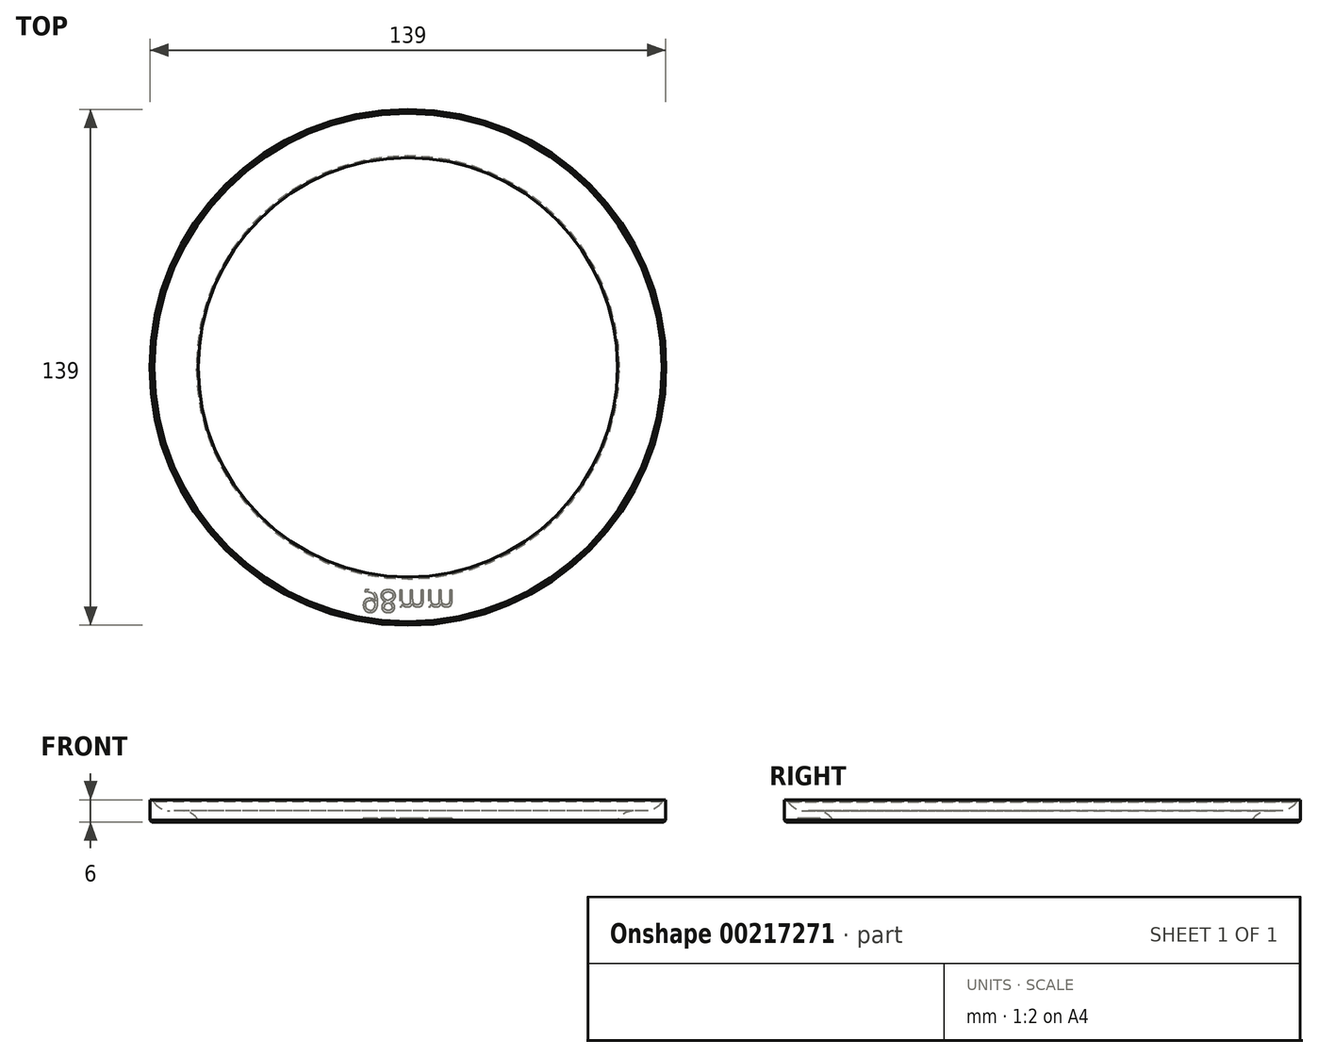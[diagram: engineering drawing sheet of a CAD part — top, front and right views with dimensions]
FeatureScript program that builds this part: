
annotation { "Feature Type Name" : "Feature", "Feature Type Description" : "" }
export const myFeature = defineFeature(function(context is Context, id is Id, definition is map)
    precondition{}
    {
        {
            var Q0;
            Q0=qCreatedBy(makeId("Front.planeOp"),FACE);
            var sketch = newSketch(context, id + "F0", { "sketchPlane" : qUnion([Q0])});
            skLineSegment(sketch, "E0", {"start": v(-69.5, 6) * mm, "end": v(-69.5, 0) * mm});
            skLineSegment(sketch, "E1", {"start": v(-69.5, 0) * mm, "end": v(-56.5, 0) * mm});
            skLineSegment(sketch, "E2", {"start": v(-56.5, 0) * mm, "end": v(-56.5, 3) * mm});
            skLineSegment(sketch, "E3", {"start": v(-56.5, 3) * mm, "end": v(-68.5, 3) * mm});
            skLineSegment(sketch, "E4", {"start": v(-68.5, 3) * mm, "end": v(-68.5, 6) * mm});
            skLineSegment(sketch, "E5", {"start": v(-68.5, 6) * mm, "end": v(-69.5, 6) * mm});
            skLineSegment(sketch, "E6", {"start": v(0, 62.77) * mm, "end": v(0, -27.64) * mm, "construction": true});
            skSolve(sketch);
        }
        {
            var Q0;
            Q0=qSketchRegion(id+"F0",true);
            var Q1;
            Q1=qSketchRegion(id+"F3",true);
            var Q2;
            Q2=sQuery(id+"F0.wireOp",EDGE,"E6");
            revolve(context, id + "F1", {"surfaceOperationType" : NewSurfaceOperationType.NEW, "entities" : qUnion([Q0, Q1]), "axis" : qUnion([Q2]), "revolveType" : RevolveType.FULL});
        }
        {
            var Q0;
            Q0=makeQuery(id+"F1.opRevolve","SWEPT_FACE",FACE,{"disambiguationData":[OSD([sQuery(id+"F0.wireOp",EDGE,"E1")])]});
            var Q1;
            Q1=makeQuery(id+"F1.opRevolve","SWEPT_EDGE",EDGE,{"disambiguationData":[OSD([sQuery(id+"F0.wireOp",EDGE,"E4"),sQuery(id+"F0.wireOp",EDGE,"E5")])]});
            chamfer(context, id + "F2", {"entities" : qUnion([Q0, Q1]), "width" : .5 * mm, "tangentPropagation" : true});
        }
        {
            var Q0;
            Q0=makeQuery(id+"F1.opRevolve","SWEPT_FACE",FACE,{"disambiguationData":[OSD([sQuery(id+"F0.wireOp",EDGE,"E1")])]});
            var sketch = newSketch(context, id + "F3", { "sketchPlane" : qUnion([Q0])});
            skText(sketch, "E7", { "text": "98mm", "fontName": "OpenSans-Regular.ttf"});
            skCircle(sketch, "E8", {"center": v(0, 0) * mm, "radius": 60 * mm, "construction": true});
            const initialGuessF3  = {"E7": [-0.01245, 0.06, 1, 0, 0.006]};
            skSetInitialGuess(sketch, initialGuessF3);
            skSolve(sketch);
        }
        {
            var Q0;
            Q0=qSketchRegion(id+"F3",true);
            var Q1;
            Q1=makeQuery(id+"F1.opRevolve","SWEPT_FACE",FACE,{"disambiguationData":[OSD([sQuery(id+"F0.wireOp",EDGE,"E5")])]});
            extrude(context, id + "F4", {"entities" : qUnion([Q0, Q1]), "operationType" : NewBodyOperationType.REMOVE, "oppositeDirection" : true, "depth" : 1 * mm, "offsetDistance" : 25 * mm});
        }
        {
            var Q0;
            Q0=makeQuery(id+"F1.opRevolve","SWEPT_FACE",FACE,{"disambiguationData":[OSD([sQuery(id+"F0.wireOp",EDGE,"E3")])]});
            fillet(context, id + "F5", {"entities" : qUnion([Q0]), "radius" : 5 * mm, "tangentPropagation" : true, "allowEdgeOverflow" : false});
        }
    });
